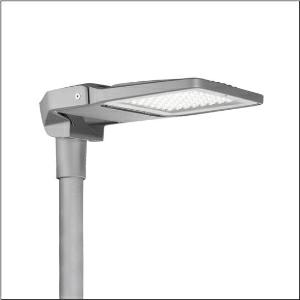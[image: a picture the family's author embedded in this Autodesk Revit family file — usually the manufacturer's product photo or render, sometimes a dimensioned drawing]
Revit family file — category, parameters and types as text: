
# Revit family: floodlight_fl_20_mini___pl43_5xa7672c1a4ac_7634
name_source: partatom
category: Lighting Fixtures
units: mm (PartAtom-declared; Revit-internal decimal feet)

## family parameters
Cut with Voids When Loaded = No
Host = Face
Light Source = No
Part Type = Normal
Room Calculation Point = No
Round Connector Dimension = Use Diameter
Shared = No

## types (1)
- --- (1 x LED 3000K / CRI = 80 (unbekannt), 10230 lm, 3000K)
    Apparent Load = 96 VA
    CIE Flux Codes = 32 74 99 100 100
    Color Rendering = 80
    Color Temperature = 3000K
    Default Elevation = 1800 mm
    Description = Floodlight FL 20 mini, floodlight, primary light control with lens, of plastic, primary optical cover: protective disc, of toughened safety glass, transparent, light distribution: PL43, light emission: direct distribution, primary light characteristic: asymmetric, installation type: side-entry, post-top, LED, High Power LED, rated luminous flux: 10.230lm, luminous efficacy: 107lm/W, light colour: 830, colour temperature: 3000K, control gear: ECG Plus, control: flexible luminous flux parameterisation, time-dependent luminous flux control, digital communication interface, overheat protection, power reduction, electronic power reduction, with terminal, 5-pole, max. 2.5mm², mains connection: 220..240V, AC, 50/60Hz, rated input power: 96W, LED unit, of diecast aluminium, powder-coated, Siteco® metallic grey (DB 702S), corrosivity category C5 mid according to DIN EN ISO 12944, incl. 1x M20 cable gland for cable Ø 6.5..12mm, inclination adjustable: 0°, 5°, 10°, 15°, please order mast flange separately, length: 565mm, width: 335mm, height: 119mm, housing frame, of diecast aluminium, powder-coated, Siteco® metallic grey (DB 702S), mast flange adapter, of diecast aluminium, powder-coated, Siteco® metallic grey (DB 702S), DALI, protection rating (complete): IP66, insulation class (complete): insulation class II (safety insulation), certification: CE, ENEC, VDE, protection symbol: D, permissible operating ambient temperature: -40..+40°C, permissible operating ambient temperature for outdoor applications: -40..+50°C, standard: DIN EN 12944, packaging unit: 1 piece

Light Distribution: PL43
    Height = 62 mm  [stored 0.203412 ft]
    Lamp = 1 x LED 3000K / CRI >= 80 (unbekannt)
    Lamp Light Flux = 10230 lm
    Lamp count = 1
    Length = 565 mm
    Luminous efficacy = 107 lm/W
    Manufacturer = Siteco
    ModVariant = No
    Model = 5XA7672C1A4AC
    Number of Poles = 1
    OnlyDefault = Yes
    Power Factor = 1
    Product Name = Floodlight FL 20 mini | PL43
    Product group = floodlight | pylon top
    ProductGroupID = 6101
    Protection Class = Protection class II
    Protection Degree = IP 66
    RLX_Detail_Level = 1
    RLX_Emergency_Light_Flux = 0 lm
    RLX_Emergency_Type = 0
    RLX_Emergency_Type_DB = No
    RlxData = <blob elided: 101857 chars, md5=95053022>
    Socket = socket
    Standby Power = 0 W
    System Light Flux = 10230 lm
    System Power = 96 W
    Type Comments = factory setting: luminous flux: 100 % | dim-lin: 254 | 500 mA
    Type Image = l_1005946.jpg
    URL = http://relux.com
    VarID = @adj_164069
    Voltage = 0 V
    Weight = 0.00 kg
    Width = 335 mm

note: [stored X ft] marks values corroborated as IEEE doubles in the binary element streams (Revit-internal decimal feet)

## geometry (parser evidence)
native form markers: Blend x4, Sweep x14
no freeform markers — native parametric forms only
